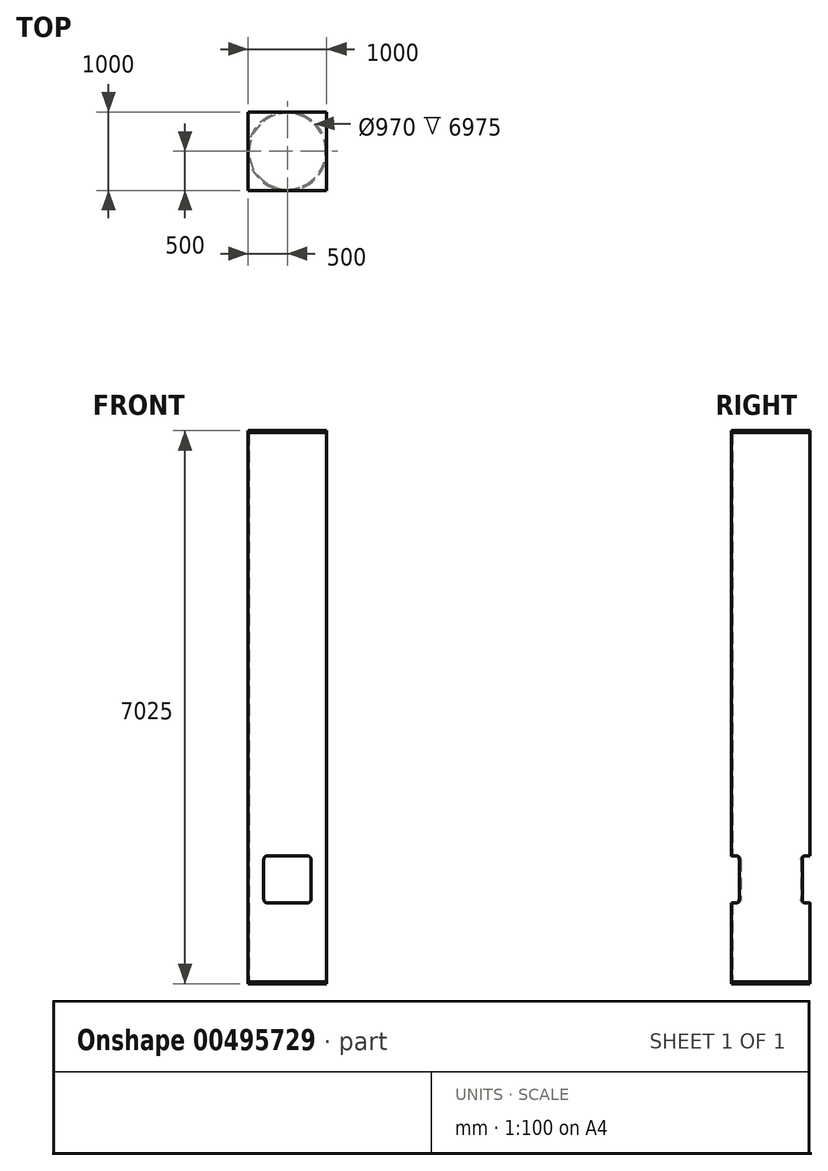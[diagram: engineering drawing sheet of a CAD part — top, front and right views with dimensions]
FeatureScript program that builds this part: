
annotation { "Feature Type Name" : "Feature", "Feature Type Description" : "" }
export const myFeature = defineFeature(function(context is Context, id is Id, definition is map)
    precondition{}
    {
        {
            var Q0;
            Q0=qCreatedBy(makeId("Top.planeOp"),FACE);
            var sketch = newSketch(context, id + "F0", { "sketchPlane" : qUnion([Q0])});
            skCircle(sketch, "E0", {"center": v(0, 0) * mm, "radius": 500 * mm});
            skCircle(sketch, "E1", {"center": v(0, 0) * mm, "radius": 485 * mm});
            skCircle(sketch, "E2", {"center": v(0, 0) * mm, "radius": 226.54 * mm});
            skSolve(sketch);
        }
        {
            var Q0;
            Q0=makeQuery(id+"F0.imprint","IMPRINT",FACE,{"disambiguationData":[TD([[makeQuery(id+"F0.imprint","IMPRINT",EDGE,{"derivedFrom":sQuery(id+"F0.wireOp",EDGE,"E0")}),1.0]])]});
            var sketch = newSketch(context, id + "F1", { "sketchPlane" : qUnion([Q0])});
            skSolve(sketch);
        }
        {
            var Q0;
            Q0=makeQuery(id+"F0.imprint","IMPRINT",FACE,{"disambiguationData":[TD([[makeQuery(id+"F0.imprint","IMPRINT",EDGE,{"derivedFrom":sQuery(id+"F0.wireOp",EDGE,"E0")}),1.0]])]});
            var Q1;
            Q1=sQuery(id+"F0.wireOp",EDGE,"E2");
            var Q2;
            Q2=sQuery(id+"F0.wireOp",EDGE,"E1");
            var Q3;
            Q3=sQuery(id+"F0.wireOp",EDGE,"E0");
            extrude(context, id + "F2", {"entities" : qUnion([Q0]), "surfaceEntities" : qUnion([Q1, Q2, Q3]), "depth" : 7000 * mm});
        }
        {
            var Q0;
            Q0=makeQuery(id+"F1.imprint","IMPRINT",FACE,{"disambiguationData":[TD([[makeQuery(id+"F1.imprint","IMPRINT",EDGE,{"derivedFrom":makeQuery(id+"F0.imprint","IMPRINT",EDGE,{"derivedFrom":sQuery(id+"F0.wireOp",EDGE,"E0")})}),1.0]])]});
            var sketch = newSketch(context, id + "F3", { "sketchPlane" : qUnion([Q0])});
            skLineSegment(sketch, "E3.bottom", {"start": v(-500, -500) * mm, "end": v(500, -500) * mm});
            skLineSegment(sketch, "E3.top", {"start": v(-500, 500) * mm, "end": v(500, 500) * mm});
            skLineSegment(sketch, "E3.left", {"start": v(-500, -500) * mm, "end": v(-500, 500) * mm});
            skLineSegment(sketch, "E3.right", {"start": v(500, -500) * mm, "end": v(500, 500) * mm});
            skSolve(sketch);
        }
        {
            var Q0;
            {var subQ0=sQuery(id+"F3.wireOp",EDGE,"E3.left");var subQ1=sQuery(id+"F3.wireOp",EDGE,"E3.bottom");var subQ2=makeQuery(id+"F3.imprint","INTERSECT",VERTEX,{"derivedFrom":[subQ1,subQ0]});Q0=makeQuery(id+"F3.imprint","IMPRINT",FACE,{"disambiguationData":[TD([[makeQuery(id+"F3.imprint","IMPRINT",EDGE,{"disambiguationData":[TD([[subQ2,-1.0]])],"derivedFrom":subQ1}),1.0]])]});}
            var Q1;
            {var subQ0=sQuery(id+"F3.wireOp",EDGE,"E3.right");var subQ1=sQuery(id+"F3.wireOp",EDGE,"E3.bottom");var subQ2=makeQuery(id+"F3.imprint","INTERSECT",VERTEX,{"derivedFrom":[subQ1,subQ0]});Q1=makeQuery(id+"F3.imprint","IMPRINT",FACE,{"disambiguationData":[TD([[makeQuery(id+"F3.imprint","IMPRINT",EDGE,{"disambiguationData":[TD([[subQ2,1.0]])],"derivedFrom":subQ1}),1.0]])]});}
            var Q2;
            {var subQ0=sQuery(id+"F3.wireOp",EDGE,"E3.right");var subQ1=sQuery(id+"F3.wireOp",EDGE,"E3.top");var subQ2=makeQuery(id+"F3.imprint","INTERSECT",VERTEX,{"derivedFrom":[subQ1,subQ0]});Q2=makeQuery(id+"F3.imprint","IMPRINT",FACE,{"disambiguationData":[TD([[makeQuery(id+"F3.imprint","IMPRINT",EDGE,{"disambiguationData":[TD([[subQ2,1.0]])],"derivedFrom":subQ1}),-1.0]])]});}
            var Q3;
            {var subQ0=sQuery(id+"F3.wireOp",EDGE,"E3.left");var subQ1=sQuery(id+"F3.wireOp",EDGE,"E3.top");var subQ2=makeQuery(id+"F3.imprint","INTERSECT",VERTEX,{"derivedFrom":[subQ1,subQ0]});Q3=makeQuery(id+"F3.imprint","IMPRINT",FACE,{"disambiguationData":[TD([[makeQuery(id+"F3.imprint","IMPRINT",EDGE,{"disambiguationData":[TD([[subQ2,-1.0]])],"derivedFrom":subQ1}),-1.0]])]});}
            var Q4;
            Q4=makeQuery(id+"F1.imprint","IMPRINT",FACE,{"disambiguationData":[TD([[makeQuery(id+"F1.imprint","IMPRINT",EDGE,{"derivedFrom":makeQuery(id+"F0.imprint","IMPRINT",EDGE,{"derivedFrom":sQuery(id+"F0.wireOp",EDGE,"E1")})}),1.0]])]});
            extrude(context, id + "F4", {"entities" : qUnion([Q0, Q1, Q2, Q3, Q4]), "operationType" : NewBodyOperationType.ADD, "depth" : 25 * mm});
        }
        {
            var Q0;
            Q0=qCreatedBy(makeId("Front.planeOp"),FACE);
            var sketch = newSketch(context, id + "F5", { "sketchPlane" : qUnion([Q0])});
            skLineSegment(sketch, "E4.bottom", {"start": v(-250, 1625) * mm, "end": v(250, 1625) * mm});
            skLineSegment(sketch, "E4.top", {"start": v(-250, 1025) * mm, "end": v(250, 1025) * mm});
            skLineSegment(sketch, "E4.left", {"start": v(-300, 1575) * mm, "end": v(-300, 1075) * mm});
            skLineSegment(sketch, "E4.right", {"start": v(300, 1575) * mm, "end": v(300, 1075) * mm});
            skPoint(sketch, "E5.visualSharp", {"position": v(-300, 1025) * mm});
            skArc(sketch, "E5.filletArc", {"start": v(-300, 1075) * mm, "mid": v(-285.36, 1039.64) * mm, "end": v(-250, 1025) * mm});
            skPoint(sketch, "E6.visualSharp", {"position": v(300, 1025) * mm});
            skArc(sketch, "E6.filletArc", {"start": v(250, 1025) * mm, "mid": v(285.36, 1039.64) * mm, "end": v(300, 1075) * mm});
            skPoint(sketch, "E7.visualSharp", {"position": v(300, 1625) * mm});
            skArc(sketch, "E7.filletArc", {"start": v(300, 1575) * mm, "mid": v(285.36, 1610.36) * mm, "end": v(250, 1625) * mm});
            skPoint(sketch, "E8.visualSharp", {"position": v(-300, 1625) * mm});
            skArc(sketch, "E8.filletArc", {"start": v(-250, 1625) * mm, "mid": v(-285.36, 1610.36) * mm, "end": v(-300, 1575) * mm});
            skSolve(sketch);
        }
        {
            var Q0;
            Q0=qSketchRegion(id+"F5",true);
            extrude(context, id + "F6", {"entities" : qUnion([Q0]), "operationType" : NewBodyOperationType.REMOVE, "endBound" : BoundingType.SYMMETRIC, "oppositeDirection" : true, "depth" : 1000 * mm});
        }
        {
            var Q0;
            Q0=makeQuery(id+"F2.opExtrude","CAP_FACE",FACE,{"disambiguationData":[OSD([sQuery(id+"F0.wireOp",EDGE,"E0"),sQuery(id+"F0.wireOp",EDGE,"E1")])],"isStart":false});
            var sketch = newSketch(context, id + "F7", { "sketchPlane" : qUnion([Q0])});
            skLineSegment(sketch, "E9.bottom", {"start": v(-500, 500) * mm, "end": v(500, 500) * mm});
            skLineSegment(sketch, "E9.top", {"start": v(-500, -500) * mm, "end": v(500, -500) * mm});
            skLineSegment(sketch, "E9.left", {"start": v(-500, 500) * mm, "end": v(-500, -500) * mm});
            skLineSegment(sketch, "E9.right", {"start": v(500, 500) * mm, "end": v(500, -500) * mm});
            skSolve(sketch);
        }
        {
            var Q0;
            Q0=makeQuery(id+"F7.imprint","IMPRINT",FACE,{"disambiguationData":[TD([[makeQuery(id+"F7.imprint","IMPRINT",EDGE,{"derivedFrom":makeQuery(id+"F2.opExtrude","CAP_EDGE",EDGE,{"disambiguationData":[OSD([sQuery(id+"F0.wireOp",EDGE,"E1")])],"isStart":false})}),1.0]])]});
            var Q1;
            {var subQ0=sQuery(id+"F7.wireOp",EDGE,"E9.right");var subQ1=sQuery(id+"F7.wireOp",EDGE,"E9.top");var subQ2=makeQuery(id+"F7.imprint","INTERSECT",VERTEX,{"derivedFrom":[subQ1,subQ0]});Q1=makeQuery(id+"F7.imprint","IMPRINT",FACE,{"disambiguationData":[TD([[makeQuery(id+"F7.imprint","IMPRINT",EDGE,{"disambiguationData":[TD([[subQ2,1.0]])],"derivedFrom":subQ1}),1.0]])]});}
            var Q2;
            {var subQ0=sQuery(id+"F7.wireOp",EDGE,"E9.left");var subQ1=sQuery(id+"F7.wireOp",EDGE,"E9.top");var subQ2=makeQuery(id+"F7.imprint","INTERSECT",VERTEX,{"derivedFrom":[subQ1,subQ0]});Q2=makeQuery(id+"F7.imprint","IMPRINT",FACE,{"disambiguationData":[TD([[makeQuery(id+"F7.imprint","IMPRINT",EDGE,{"disambiguationData":[TD([[subQ2,-1.0]])],"derivedFrom":subQ1}),1.0]])]});}
            var Q3;
            {var subQ0=sQuery(id+"F7.wireOp",EDGE,"E9.right");var subQ1=sQuery(id+"F7.wireOp",EDGE,"E9.bottom");var subQ2=makeQuery(id+"F7.imprint","INTERSECT",VERTEX,{"derivedFrom":[subQ1,subQ0]});Q3=makeQuery(id+"F7.imprint","IMPRINT",FACE,{"disambiguationData":[TD([[makeQuery(id+"F7.imprint","IMPRINT",EDGE,{"disambiguationData":[TD([[subQ2,1.0]])],"derivedFrom":subQ1}),-1.0]])]});}
            var Q4;
            {var subQ0=sQuery(id+"F7.wireOp",EDGE,"E9.left");var subQ1=sQuery(id+"F7.wireOp",EDGE,"E9.bottom");var subQ2=makeQuery(id+"F7.imprint","INTERSECT",VERTEX,{"derivedFrom":[subQ1,subQ0]});Q4=makeQuery(id+"F7.imprint","IMPRINT",FACE,{"disambiguationData":[TD([[makeQuery(id+"F7.imprint","IMPRINT",EDGE,{"disambiguationData":[TD([[subQ2,-1.0]])],"derivedFrom":subQ1}),-1.0]])]});}
            var Q5;
            Q5=makeQuery(id+"F2.opExtrude","CAP_FACE",FACE,{"disambiguationData":[OSD([sQuery(id+"F0.wireOp",EDGE,"E0"),sQuery(id+"F0.wireOp",EDGE,"E1")])],"isStart":false});
            var Q6;
            Q6=makeQuery(id+"F7.imprint","IMPRINT",FACE,{"disambiguationData":[TD([[makeQuery(id+"F7.imprint","IMPRINT",EDGE,{"derivedFrom":makeQuery(id+"F2.opExtrude","CAP_EDGE",EDGE,{"disambiguationData":[OSD([sQuery(id+"F0.wireOp",EDGE,"E1")])],"isStart":false})}),-1.0]])]});
            extrude(context, id + "F8", {"entities" : qUnion([Q0, Q1, Q2, Q3, Q4, Q5, Q6]), "operationType" : NewBodyOperationType.ADD, "depth" : 25 * mm});
        }
    });
